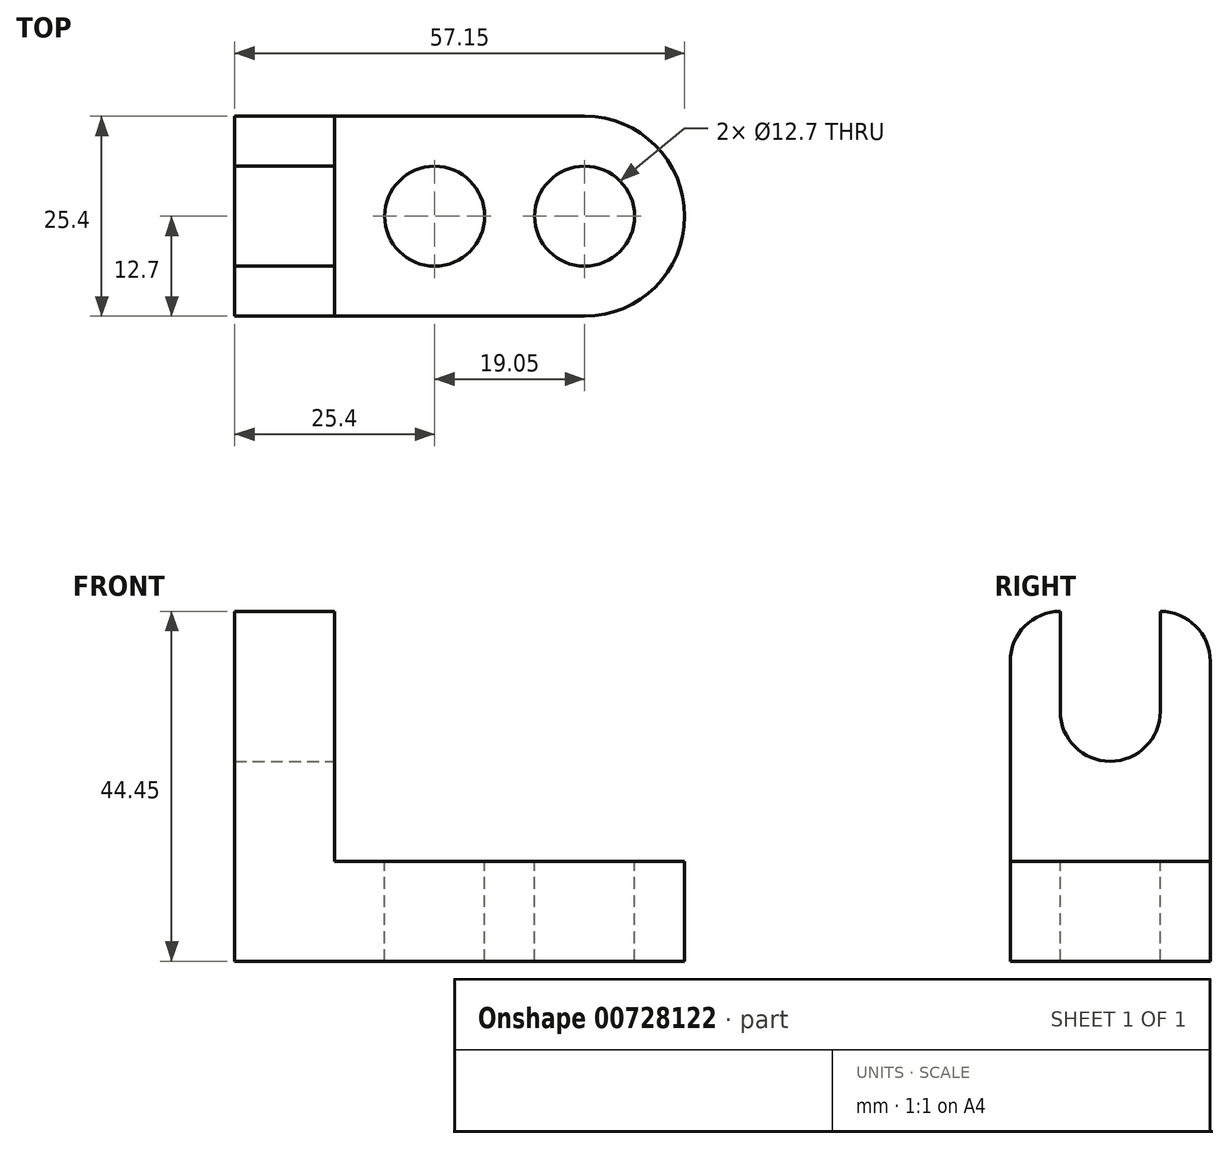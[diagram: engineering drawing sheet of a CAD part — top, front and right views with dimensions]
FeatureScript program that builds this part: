
annotation { "Feature Type Name" : "Feature", "Feature Type Description" : "" }
export const myFeature = defineFeature(function(context is Context, id is Id, definition is map)
    precondition{}
    {
        {
            var Q0;
            Q0=qCreatedBy(makeId("Front.planeOp"),FACE);
            var sketch = newSketch(context, id + "F0", { "sketchPlane" : qUnion([Q0])});
            skLineSegment(sketch, "E0", {"start": v(0, 0) * mm, "end": v(57.15, 0) * mm});
            skLineSegment(sketch, "E1", {"start": v(57.15, 0) * mm, "end": v(57.15, 44.45) * mm});
            skLineSegment(sketch, "E2", {"start": v(57.15, 44.45) * mm, "end": v(0, 44.45) * mm});
            skLineSegment(sketch, "E3", {"start": v(0, 44.45) * mm, "end": v(0, 0) * mm});
            skSolve(sketch);
        }
        {
            var Q0;
            Q0=makeQuery(id+"F0.imprint","IMPRINT",FACE,{"disambiguationData":[TD([[makeQuery(id+"F0.imprint","IMPRINT",EDGE,{"derivedFrom":sQuery(id+"F0.wireOp",EDGE,"E0")}),1.0]])]});
            extrude(context, id + "F1", {"entities" : qUnion([Q0]), "depth" : 25.4 * mm, "offsetDistance" : 25.4 * mm});
        }
        {
            var Q0;
            Q0=makeQuery(id+"F1.opExtrude","CAP_FACE",FACE,{"disambiguationData":[OSD([sQuery(id+"F0.wireOp",EDGE,"E0"),sQuery(id+"F0.wireOp",EDGE,"E1"),sQuery(id+"F0.wireOp",EDGE,"E2"),sQuery(id+"F0.wireOp",EDGE,"E3")])],"isStart":false});
            var sketch = newSketch(context, id + "F2", { "sketchPlane" : qUnion([Q0])});
            skLineSegment(sketch, "E4", {"start": v(12.7, 44.45) * mm, "end": v(12.7, 12.7) * mm});
            skLineSegment(sketch, "E5", {"start": v(12.7, 12.7) * mm, "end": v(57.15, 12.7) * mm});
            skSolve(sketch);
        }
        {
            var Q0;
            {var subQ0=sQuery(id+"F2.wireOp",EDGE,"E4");Q0=makeQuery(id+"F2.imprint","IMPRINT",FACE,{"disambiguationData":[TD([[makeQuery(id+"F2.imprint","IMPRINT",EDGE,{"derivedFrom":subQ0}),1.0]])]});}
            extrude(context, id + "F3", {"entities" : qUnion([Q0]), "operationType" : NewBodyOperationType.REMOVE, "oppositeDirection" : true, "depth" : 25.4 * mm, "offsetDistance" : 25.4 * mm});
        }
        {
            var Q0;
            Q0=makeQuery(id+"F3.boolean.opBoolean","COPY",FACE,{"derivedFrom":makeQuery(id+"F3.opExtrude","SWEPT_FACE",FACE,{"disambiguationData":[OSD([sQuery(id+"F2.wireOp",EDGE,"E5")])]})});
            var sketch = newSketch(context, id + "F4", { "sketchPlane" : qUnion([Q0])});
            skCircle(sketch, "E6", {"center": v(25.4, -12.7) * mm, "radius": 6.35 * mm});
            skCircle(sketch, "E7", {"center": v(44.45, -12.7) * mm, "radius": 6.35 * mm});
            skArc(sketch, "E8", {"start": v(44.45, -25.4) * mm, "mid": v(57.15, -12.7) * mm, "end": v(44.45, 0) * mm});
            skSolve(sketch);
        }
        {
            var Q0;
            Q0=makeQuery(id+"F4.imprint","IMPRINT",FACE,{"disambiguationData":[TD([[makeQuery(id+"F4.imprint","IMPRINT",EDGE,{"derivedFrom":sQuery(id+"F4.wireOp",EDGE,"E6")}),1.0]])]});
            var Q1;
            Q1=makeQuery(id+"F4.imprint","IMPRINT",FACE,{"disambiguationData":[TD([[makeQuery(id+"F4.imprint","IMPRINT",EDGE,{"derivedFrom":sQuery(id+"F4.wireOp",EDGE,"E7")}),1.0]])]});
            var Q2;
            {var subQ0=sQuery(id+"F4.wireOp",EDGE,"E8");var subQ1=sQuery(id+"F2.wireOp",EDGE,"E5");var subQ2=makeQuery(id+"F3.boolean.opBoolean","COPY",EDGE,{"derivedFrom":makeQuery(id+"F3.opExtrude","CAP_EDGE",EDGE,{"disambiguationData":[OSD([subQ1])],"isStart":true})});var subQ3=makeQuery(id+"F4.imprint","INTERSECT",VERTEX,{"derivedFrom":[subQ2,subQ0]});Q2=makeQuery(id+"F4.imprint","IMPRINT",FACE,{"disambiguationData":[TD([[makeQuery(id+"F4.imprint","IMPRINT",EDGE,{"disambiguationData":[TD([[subQ3,-1.0]])],"derivedFrom":subQ0}),-1.0]])]});}
            var Q3;
            {var subQ0=sQuery(id+"F4.wireOp",EDGE,"E8");var subQ1=sQuery(id+"F2.wireOp",EDGE,"E5");var subQ2=makeQuery(id+"F3.boolean.opBoolean","COPY",EDGE,{"derivedFrom":makeQuery(id+"F3.opExtrude","CAP_EDGE",EDGE,{"disambiguationData":[OSD([subQ1])],"isStart":false})});var subQ3=makeQuery(id+"F4.imprint","INTERSECT",VERTEX,{"derivedFrom":[subQ2,subQ0]});Q3=makeQuery(id+"F4.imprint","IMPRINT",FACE,{"disambiguationData":[TD([[makeQuery(id+"F4.imprint","IMPRINT",EDGE,{"disambiguationData":[TD([[subQ3,1.0]])],"derivedFrom":subQ0}),-1.0]])]});}
            extrude(context, id + "F5", {"entities" : qUnion([Q0, Q1, Q2, Q3]), "operationType" : NewBodyOperationType.REMOVE, "oppositeDirection" : true, "depth" : 12.7 * mm, "offsetDistance" : 25.4 * mm});
        }
        {
            var Q0;
            Q0=makeQuery(id+"F3.boolean.opBoolean","COPY",FACE,{"derivedFrom":makeQuery(id+"F3.opExtrude","SWEPT_FACE",FACE,{"disambiguationData":[OSD([sQuery(id+"F2.wireOp",EDGE,"E4")])]})});
            var sketch = newSketch(context, id + "F6", { "sketchPlane" : qUnion([Q0])});
            skCircle(sketch, "E9", {"center": v(-12.7, 31.75) * mm, "radius": 6.35 * mm});
            skLineSegment(sketch, "E10", {"start": v(-19.05, 31.75) * mm, "end": v(-19.05, 44.45) * mm});
            skLineSegment(sketch, "E11", {"start": v(-6.35, 31.75) * mm, "end": v(-6.35, 44.45) * mm});
            skArc(sketch, "E12", {"start": v(-19.05, 44.45) * mm, "mid": v(-23.54, 42.6) * mm, "end": v(-25.4, 38.1) * mm});
            skArc(sketch, "E13", {"start": v(0, 38.1) * mm, "mid": v(-1.86, 42.6) * mm, "end": v(-6.35, 44.45) * mm});
            skSolve(sketch);
        }
        {
            var Q0;
            {var subQ0=sQuery(id+"F6.wireOp",EDGE,"E12");Q0=makeQuery(id+"F6.imprint","IMPRINT",FACE,{"disambiguationData":[TD([[makeQuery(id+"F6.imprint","IMPRINT",EDGE,{"derivedFrom":subQ0}),-1.0]])]});}
            var Q1;
            {var subQ0=sQuery(id+"F6.wireOp",EDGE,"E10");Q1=makeQuery(id+"F6.imprint","IMPRINT",FACE,{"disambiguationData":[TD([[makeQuery(id+"F6.imprint","IMPRINT",EDGE,{"derivedFrom":subQ0}),-1.0]])]});}
            var Q2;
            {var subQ0=sQuery(id+"F6.wireOp",EDGE,"E9");var subQ1=makeQuery(id+"F6.imprint","INTERSECT",VERTEX,{"derivedFrom":[subQ0,sQuery(id+"F6.wireOp",EDGE,"E10")]});Q2=makeQuery(id+"F6.imprint","IMPRINT",FACE,{"disambiguationData":[TD([[makeQuery(id+"F6.imprint","IMPRINT",EDGE,{"disambiguationData":[TD([[subQ1,1.0]])],"derivedFrom":subQ0}),1.0]])]});}
            var Q3;
            {var subQ0=sQuery(id+"F6.wireOp",EDGE,"E13");Q3=makeQuery(id+"F6.imprint","IMPRINT",FACE,{"disambiguationData":[TD([[makeQuery(id+"F6.imprint","IMPRINT",EDGE,{"derivedFrom":subQ0}),-1.0]])]});}
            extrude(context, id + "F7", {"entities" : qUnion([Q0, Q1, Q2, Q3]), "operationType" : NewBodyOperationType.REMOVE, "oppositeDirection" : true, "depth" : 12.7 * mm, "offsetDistance" : 25.4 * mm});
        }
    });
